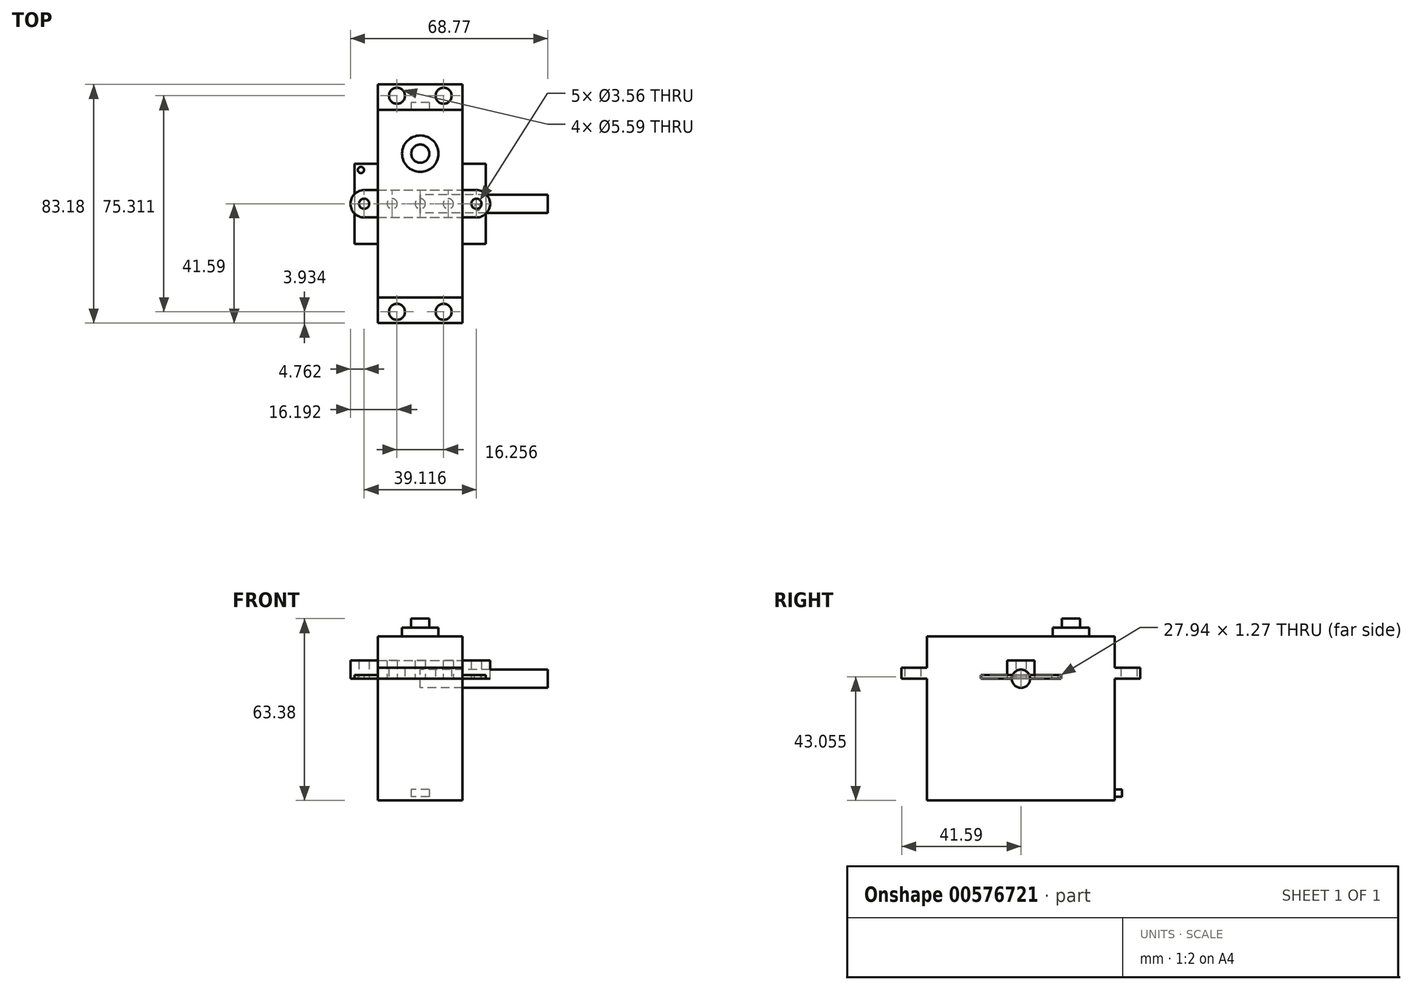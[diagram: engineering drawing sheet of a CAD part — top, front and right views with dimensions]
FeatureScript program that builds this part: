
annotation { "Feature Type Name" : "Feature", "Feature Type Description" : "" }
export const myFeature = defineFeature(function(context is Context, id is Id, definition is map)
    precondition{}
    {
        {
            var Q0;
            Q0=qCreatedBy(makeId("Top.planeOp"),FACE);
            var sketch = newSketch(context, id + "F0", { "sketchPlane" : qUnion([Q0])});
            skLineSegment(sketch, "E0.bottom", {"start": v(-22.86, 13.97) * mm, "end": v(22.86, 13.97) * mm});
            skLineSegment(sketch, "E0.top", {"start": v(-22.86, -13.97) * mm, "end": v(22.86, -13.97) * mm});
            skLineSegment(sketch, "E0.left", {"start": v(-22.86, 13.97) * mm, "end": v(-22.86, -13.97) * mm});
            skLineSegment(sketch, "E0.right", {"start": v(22.86, 13.97) * mm, "end": v(22.86, -13.97) * mm});
            skPoint(sketch, "E0.middle", {"position": v(0, 0) * mm});
            skCircle(sketch, "E1", {"center": v(-20.68, 11.8) * mm, "radius": 1.09 * mm});
            skCircle(sketch, "E2", {"center": v(19.86, -1.27) * mm, "radius": 1.09 * mm});
            skSolve(sketch);
        }
        {
            var Q0;
            Q0=makeQuery(id+"F0.imprint","IMPRINT",FACE,{"disambiguationData":[TD([[makeQuery(id+"F0.imprint","IMPRINT",EDGE,{"derivedFrom":sQuery(id+"F0.wireOp",EDGE,"E0.bottom")}),-1.0]])]});
            extrude(context, id + "F1", {"entities" : qUnion([Q0]), "depth" : 1.27 * mm, "offsetDistance" : 25.4 * mm});
        }
        {
            var Q0;
            Q0=qCreatedBy(makeId("Top.planeOp"),FACE);
            var sketch = newSketch(context, id + "F2", { "sketchPlane" : qUnion([Q0])});
            skLineSegment(sketch, "E3.bottom", {"start": v(-14.73, 41.6) * mm, "end": v(14.73, 41.6) * mm});
            skLineSegment(sketch, "E3.top", {"start": v(-14.73, -41.6) * mm, "end": v(14.73, -41.6) * mm});
            skLineSegment(sketch, "E3.left", {"start": v(-14.73, 41.6) * mm, "end": v(-14.73, -41.6) * mm});
            skLineSegment(sketch, "E3.right", {"start": v(14.73, 41.6) * mm, "end": v(14.73, -41.6) * mm});
            skPoint(sketch, "E3.middle", {"position": v(0, 0) * mm});
            skLineSegment(sketch, "E4", {"start": v(-14.73, 32.7) * mm, "end": v(14.73, 32.7) * mm});
            skLineSegment(sketch, "E5", {"start": v(14.73, -32.7) * mm, "end": v(-14.73, -32.7) * mm});
            skCircle(sketch, "E6", {"center": v(-8.13, 37.66) * mm, "radius": 2.8 * mm});
            skCircle(sketch, "E7", {"center": v(8.13, 37.66) * mm, "radius": 2.8 * mm});
            skCircle(sketch, "E8", {"center": v(8.13, -37.66) * mm, "radius": 2.8 * mm});
            skCircle(sketch, "E9", {"center": v(-8.13, -37.66) * mm, "radius": 2.8 * mm});
            skSolve(sketch);
        }
        {
            var Q0;
            {var subQ2=sQuery(id+"F2.wireOp",EDGE,"E3.bottom");Q0=makeQuery(id+"F2.imprint","IMPRINT",FACE,{"disambiguationData":[TD([[makeQuery(id+"F2.imprint","IMPRINT",EDGE,{"derivedFrom":subQ2}),-1.0]])]});}
            var Q1;
            {var subQ0=sQuery(id+"F2.wireOp",EDGE,"E4");Q1=makeQuery(id+"F2.imprint","IMPRINT",FACE,{"disambiguationData":[TD([[makeQuery(id+"F2.imprint","IMPRINT",EDGE,{"derivedFrom":subQ0}),-1.0]])]});}
            var Q2;
            {var subQ1=sQuery(id+"F2.wireOp",EDGE,"E3.top");Q2=makeQuery(id+"F2.imprint","IMPRINT",FACE,{"disambiguationData":[TD([[makeQuery(id+"F2.imprint","IMPRINT",EDGE,{"derivedFrom":subQ1}),1.0]])]});}
            extrude(context, id + "F3", {"entities" : qUnion([Q0, Q1, Q2]), "depth" : 3.8 * mm, "offsetDistance" : 25.4 * mm});
        }
        {
            var Q0;
            {var subQ0=sQuery(id+"F2.wireOp",EDGE,"E4");Q0=makeQuery(id+"F2.imprint","IMPRINT",FACE,{"disambiguationData":[TD([[makeQuery(id+"F2.imprint","IMPRINT",EDGE,{"derivedFrom":subQ0}),-1.0]])]});}
            extrude(context, id + "F4", {"entities" : qUnion([Q0]), "operationType" : NewBodyOperationType.ADD, "depth" : 14.73 * mm, "offsetDistance" : 25.4 * mm});
        }
        {
            var Q0;
            {var subQ0=sQuery(id+"F2.wireOp",EDGE,"E4");Q0=makeQuery(id+"F2.imprint","IMPRINT",FACE,{"disambiguationData":[TD([[makeQuery(id+"F2.imprint","IMPRINT",EDGE,{"derivedFrom":subQ0}),-1.0]])]});}
            extrude(context, id + "F5", {"entities" : qUnion([Q0]), "operationType" : NewBodyOperationType.ADD, "oppositeDirection" : true, "depth" : 42.42 * mm, "offsetDistance" : 25.4 * mm});
        }
        {
            var Q0;
            Q0=makeQuery(id+"F4.opExtrude","CAP_FACE",FACE,{"disambiguationData":[OSD([sQuery(id+"F2.wireOp",EDGE,"E3.left"),sQuery(id+"F2.wireOp",EDGE,"E3.right"),sQuery(id+"F2.wireOp",EDGE,"E4"),sQuery(id+"F2.wireOp",EDGE,"E5")])],"isStart":false});
            var sketch = newSketch(context, id + "F6", { "sketchPlane" : qUnion([Q0])});
            skLineSegment(sketch, "E10", {"start": v(0, 32.7) * mm, "end": v(0, -32.7) * mm, "construction": true});
            skLineSegment(sketch, "E11", {"start": v(14.73, 17.46) * mm, "end": v(-14.73, 17.46) * mm, "construction": true});
            skCircle(sketch, "E12", {"center": v(0, 17.46) * mm, "radius": 6.35 * mm});
            skCircle(sketch, "E13", {"center": v(0, 17.46) * mm, "radius": 3.18 * mm});
            skSolve(sketch);
        }
        {
            var Q0;
            Q0=makeQuery(id+"F6.imprint","IMPRINT",FACE,{"disambiguationData":[TD([[makeQuery(id+"F6.imprint","IMPRINT",EDGE,{"derivedFrom":sQuery(id+"F6.wireOp",EDGE,"E13")}),1.0]])]});
            extrude(context, id + "F7", {"entities" : qUnion([Q0]), "operationType" : NewBodyOperationType.ADD, "depth" : 6.22 * mm, "offsetDistance" : 25.4 * mm});
        }
        {
            var Q0;
            Q0=makeQuery(id+"F6.imprint","IMPRINT",FACE,{"disambiguationData":[TD([[makeQuery(id+"F6.imprint","IMPRINT",EDGE,{"derivedFrom":sQuery(id+"F6.wireOp",EDGE,"E12")}),1.0]])]});
            extrude(context, id + "F8", {"entities" : qUnion([Q0]), "operationType" : NewBodyOperationType.ADD, "depth" : 3.05 * mm, "offsetDistance" : 25.4 * mm});
        }
        {
            var Q0;
            Q0=makeQuery(id+"F5.opExtrude","SWEPT_FACE",FACE,{"disambiguationData":[OSD([sQuery(id+"F2.wireOp",EDGE,"E4")])]});
            var sketch = newSketch(context, id + "F9", { "sketchPlane" : qUnion([Q0])});
            skLineSegment(sketch, "E14", {"start": v(0, -42.42) * mm, "end": v(0, 0) * mm, "construction": true});
            skLineSegment(sketch, "E15.bottom", {"start": v(-3.18, -38.6) * mm, "end": v(3.17, -38.6) * mm});
            skLineSegment(sketch, "E15.top", {"start": v(-3.18, -41.15) * mm, "end": v(3.17, -41.15) * mm});
            skLineSegment(sketch, "E15.left", {"start": v(-3.18, -38.6) * mm, "end": v(-3.18, -41.15) * mm});
            skLineSegment(sketch, "E15.right", {"start": v(3.17, -38.6) * mm, "end": v(3.17, -41.15) * mm});
            skPoint(sketch, "E15.middle", {"position": v(0, -39.88) * mm});
            skSolve(sketch);
        }
        {
            var Q0;
            Q0=makeQuery(id+"F9.imprint","IMPRINT",FACE,{"disambiguationData":[TD([[makeQuery(id+"F9.imprint","IMPRINT",EDGE,{"derivedFrom":sQuery(id+"F9.wireOp",EDGE,"E15.bottom")}),-1.0]])]});
            extrude(context, id + "F10", {"entities" : qUnion([Q0]), "operationType" : NewBodyOperationType.ADD, "depth" : 2.54 * mm, "offsetDistance" : 25.4 * mm});
        }
        {
            var Q0;
            Q0=qCreatedBy(makeId("Right.planeOp"),FACE);
            var sketch = newSketch(context, id + "F11", { "sketchPlane" : qUnion([Q0])});
            skCircle(sketch, "E16", {"center": v(0, 0) * mm, "radius": 3.18 * mm});
            skSolve(sketch);
        }
        {
            var Q0;
            Q0=makeQuery(id+"F11.imprint","IMPRINT",FACE,{"disambiguationData":[TD([[makeQuery(id+"F11.imprint","IMPRINT",EDGE,{"derivedFrom":sQuery(id+"F11.wireOp",EDGE,"E16")}),1.0]])]});
            extrude(context, id + "F12", {"entities" : qUnion([Q0]), "depth" : 44.45 * mm, "offsetDistance" : 25.4 * mm});
        }
        {
            var Q0;
            Q0=qCreatedBy(makeId("Top.planeOp"),FACE);
            var sketch = newSketch(context, id + "F13", { "sketchPlane" : qUnion([Q0])});
            skLineSegment(sketch, "E17.bottom", {"start": v(-24.32, 4.76) * mm, "end": v(24.32, 4.76) * mm});
            skLineSegment(sketch, "E17.top", {"start": v(-24.32, -4.76) * mm, "end": v(24.32, -4.76) * mm});
            skLineSegment(sketch, "E17.left", {"start": v(-24.32, 4.76) * mm, "end": v(-24.32, -4.76) * mm});
            skLineSegment(sketch, "E17.right", {"start": v(24.32, 4.76) * mm, "end": v(24.32, -4.76) * mm});
            skPoint(sketch, "E17.middle", {"position": v(0, 0) * mm});
            skCircle(sketch, "E18", {"center": v(0, 0) * mm, "radius": 1.78 * mm});
            skCircle(sketch, "E19", {"center": v(-9.78, 0) * mm, "radius": 1.78 * mm});
            skCircle(sketch, "E20", {"center": v(-19.56, 0) * mm, "radius": 1.78 * mm});
            skCircle(sketch, "E21", {"center": v(9.78, 0) * mm, "radius": 1.78 * mm});
            skCircle(sketch, "E22", {"center": v(19.56, 0) * mm, "radius": 1.78 * mm});
            skSolve(sketch);
        }
        {
            var Q0;
            Q0=makeQuery(id+"F13.imprint","IMPRINT",FACE,{"disambiguationData":[TD([[makeQuery(id+"F13.imprint","IMPRINT",EDGE,{"derivedFrom":sQuery(id+"F13.wireOp",EDGE,"E17.bottom")}),-1.0]])]});
            extrude(context, id + "F14", {"entities" : qUnion([Q0]), "depth" : 6.35 * mm, "offsetDistance" : 25.4 * mm});
        }
        {
            var Q0;
            Q0=makeQuery(id+"F14.opExtrude","SWEPT_EDGE",EDGE,{"disambiguationData":[OSD([sQuery(id+"F13.wireOp",EDGE,"E17.top"),sQuery(id+"F13.wireOp",EDGE,"E17.left")])]});
            var Q1;
            Q1=makeQuery(id+"F14.opExtrude","SWEPT_EDGE",EDGE,{"disambiguationData":[OSD([sQuery(id+"F13.wireOp",EDGE,"E17.top"),sQuery(id+"F13.wireOp",EDGE,"E17.right")])]});
            var Q2;
            Q2=makeQuery(id+"F14.opExtrude","SWEPT_EDGE",EDGE,{"disambiguationData":[OSD([sQuery(id+"F13.wireOp",EDGE,"E17.bottom"),sQuery(id+"F13.wireOp",EDGE,"E17.right")])]});
            var Q3;
            Q3=makeQuery(id+"F14.opExtrude","SWEPT_EDGE",EDGE,{"disambiguationData":[OSD([sQuery(id+"F13.wireOp",EDGE,"E17.bottom"),sQuery(id+"F13.wireOp",EDGE,"E17.left")])]});
            fillet(context, id + "F15", {"entities" : qUnion([Q0, Q1, Q2, Q3]), "radius" : 4.76 * mm, "tangentPropagation" : true, "allowEdgeOverflow" : false});
        }
    });
